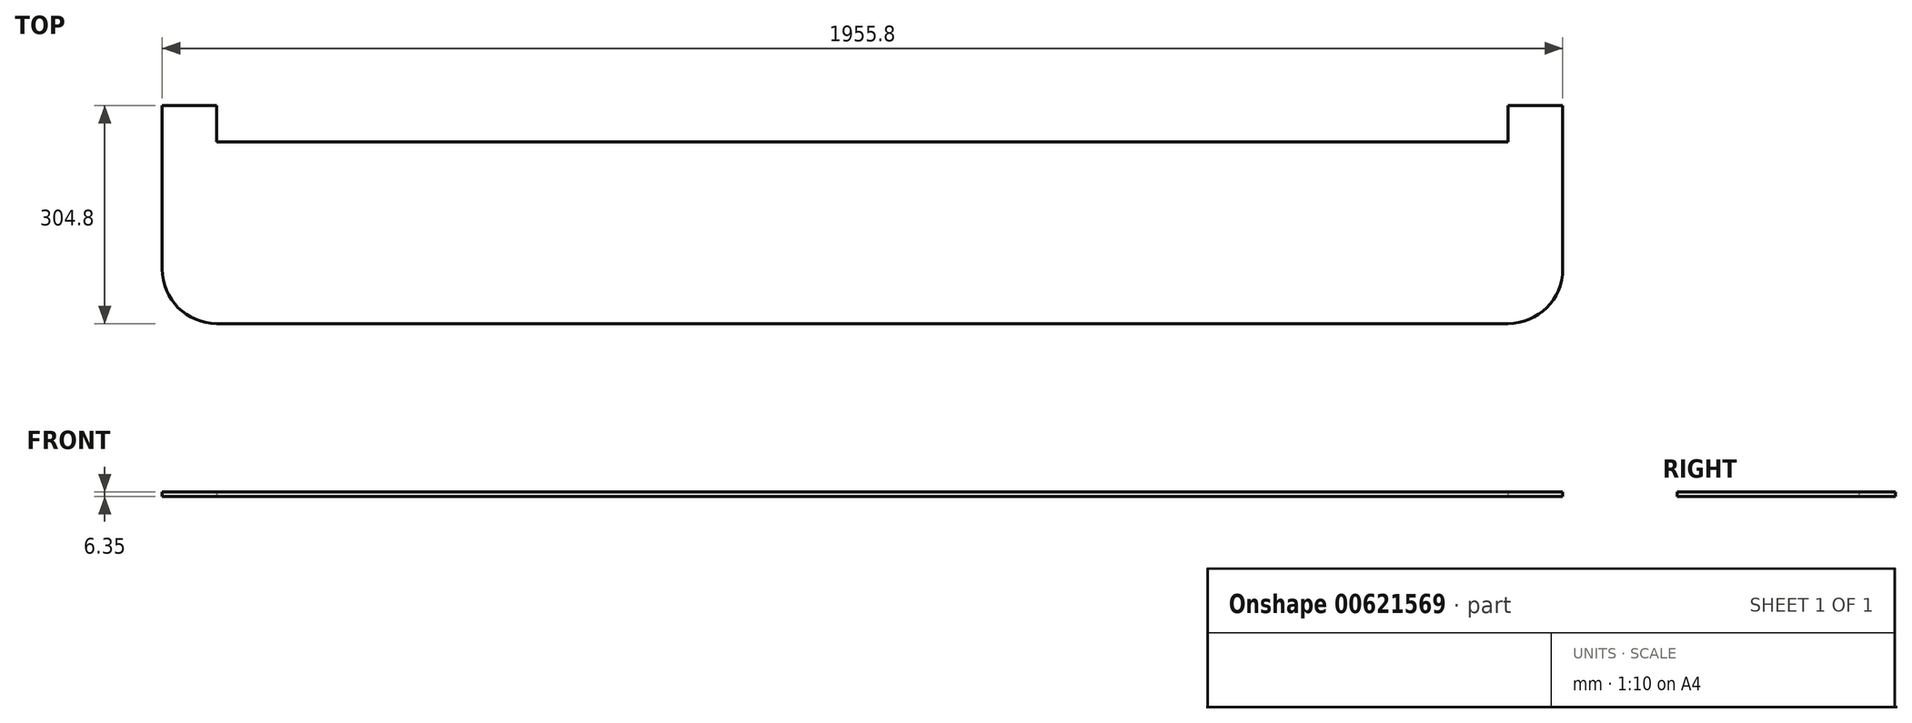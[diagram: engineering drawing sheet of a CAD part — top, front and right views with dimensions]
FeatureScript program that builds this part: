
annotation { "Feature Type Name" : "Feature", "Feature Type Description" : "" }
export const myFeature = defineFeature(function(context is Context, id is Id, definition is map)
    precondition{}
    {
        {
            var Q0;
            Q0=qCreatedBy(makeId("Top.planeOp"),FACE);
            var sketch = newSketch(context, id + "F0", { "sketchPlane" : qUnion([Q0])});
            skLineSegment(sketch, "E0.bottom", {"start": v(977.9, 152.4) * mm, "end": v(901.7, 152.4) * mm});
            skLineSegment(sketch, "E0.top", {"start": v(977.9, -152.4) * mm, "end": v(-977.9, -152.4) * mm});
            skLineSegment(sketch, "E0.left", {"start": v(977.9, 152.4) * mm, "end": v(977.9, -152.4) * mm});
            skLineSegment(sketch, "E0.right", {"start": v(-977.9, 152.4) * mm, "end": v(-977.9, -152.4) * mm});
            skPoint(sketch, "E0.middle", {"position": v(0, 0) * mm});
            skLineSegment(sketch, "E1.0", {"start": v(901.7, 101.6) * mm, "end": v(-901.7, 101.6) * mm});
            skLineSegment(sketch, "E2.0", {"start": v(-901.7, 152.4) * mm, "end": v(-901.7, 101.6) * mm});
            skLineSegment(sketch, "E3.0", {"start": v(901.7, 152.4) * mm, "end": v(901.7, 101.6) * mm});
            skLineSegment(sketch, "E4.trimOffspring", {"start": v(-901.7, 152.4) * mm, "end": v(-977.9, 152.4) * mm});
            skSolve(sketch);
        }
        {
            var Q0;
            Q0 = qSketchRegion(id + "F0", true);
            extrude(context, id + "F1", {"entities" : qUnion([Q0]), "depth" : 6.35 * mm, "offsetDistance" : 25.4 * mm});
        }
        {
            var Q0;
            Q0=makeQuery(id+"F1.opExtrude","SWEPT_EDGE",EDGE,{"disambiguationData":[OSD([sQuery(id+"F0.wireOp",EDGE,"E0.top"),sQuery(id+"F0.wireOp",EDGE,"E0.left")])]});
            var Q1;
            Q1=makeQuery(id+"F1.opExtrude","SWEPT_EDGE",EDGE,{"disambiguationData":[OSD([sQuery(id+"F0.wireOp",EDGE,"E0.top"),sQuery(id+"F0.wireOp",EDGE,"E0.right")])]});
            fillet(context, id + "F2", {"entities" : qUnion([Q0, Q1]), "radius" : 76.2 * mm, "tangentPropagation" : true, "allowEdgeOverflow" : false});
        }
    });
